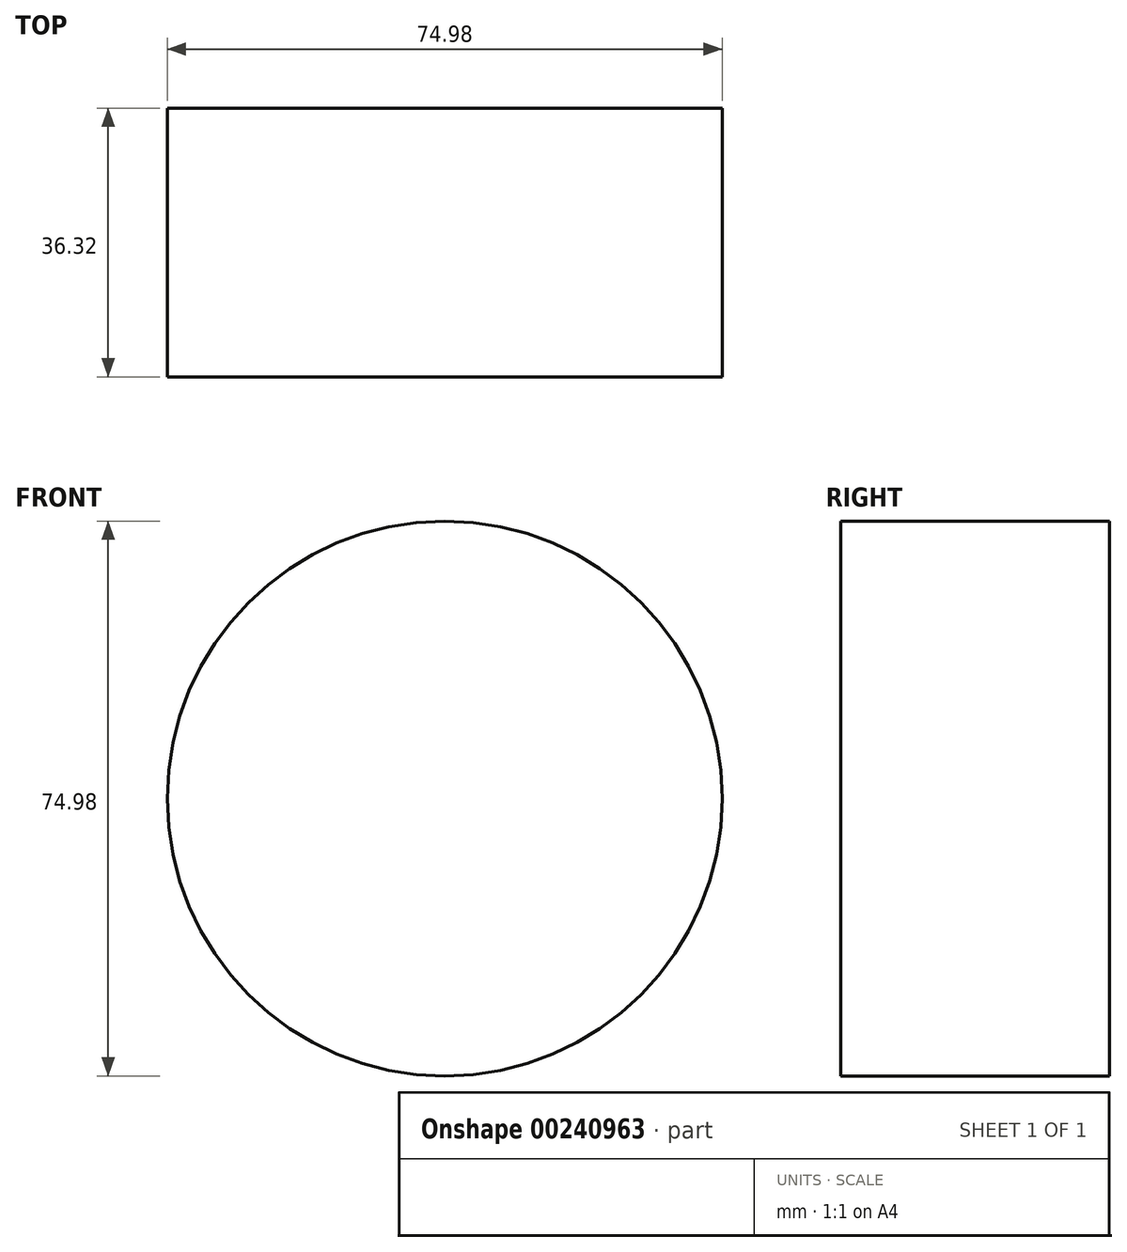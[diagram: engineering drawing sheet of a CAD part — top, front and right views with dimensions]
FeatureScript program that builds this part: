
annotation { "Feature Type Name" : "Feature", "Feature Type Description" : "" }
export const myFeature = defineFeature(function(context is Context, id is Id, definition is map)
    precondition{}
    {
        {
            var Q0;
            Q0=qCreatedBy(makeId("Front.planeOp"),FACE);
            var sketch = newSketch(context, id + "F0", { "sketchPlane" : qUnion([Q0])});
            skCircle(sketch, "E0", {"center": v(0, 0) * mm, "radius": 37.49 * mm});
            skSolve(sketch);
        }
        {
            var Q0;
            Q0=makeQuery(id+"F0.imprint","IMPRINT",FACE,{"disambiguationData":[TD([[makeQuery(id+"F0.imprint","IMPRINT",EDGE,{"derivedFrom":sQuery(id+"F0.wireOp",EDGE,"E0")}),1.0]])]});
            extrude(context, id + "F1", {"entities" : qUnion([Q0]), "depth" : 36.32 * mm});
        }
    });
